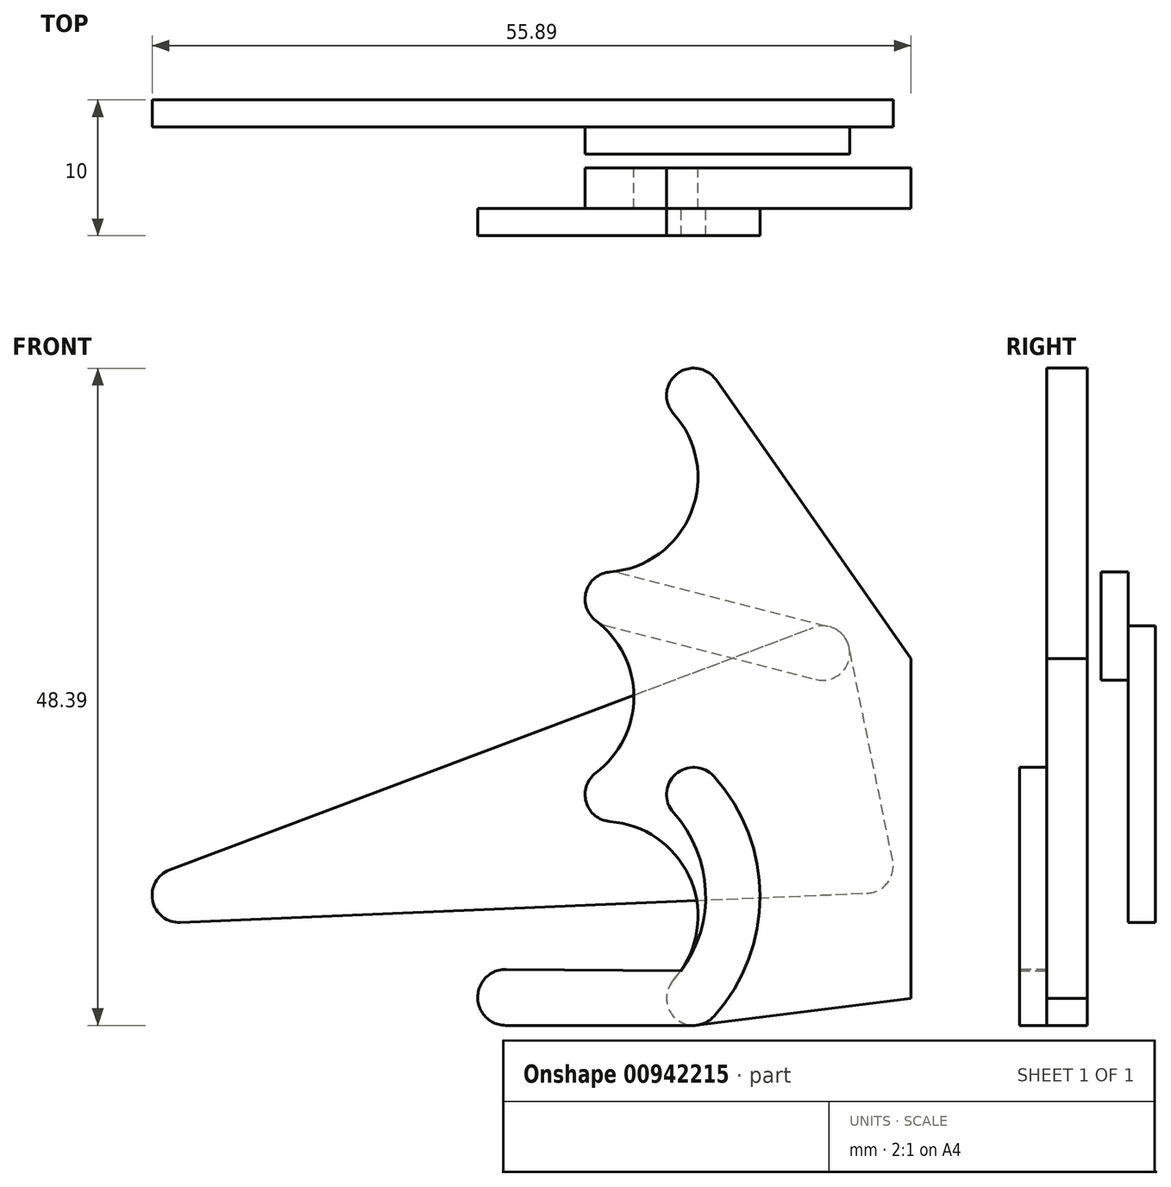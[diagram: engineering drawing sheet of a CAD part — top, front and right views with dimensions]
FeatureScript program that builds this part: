
annotation { "Feature Type Name" : "Feature", "Feature Type Description" : "" }
export const myFeature = defineFeature(function(context is Context, id is Id, definition is map)
    precondition{}
    {
        {
            var Q0;
            Q0=qCreatedBy(makeId("Front.planeOp"),FACE);
            var sketch = newSketch(context, id + "F0", { "sketchPlane" : qUnion([Q0])});
            skLineSegment(sketch, "E0", {"start": v(-16, 0) * mm, "end": v(-22, 29.4) * mm});
            skLineSegment(sketch, "E1", {"start": v(-22, 29.4) * mm, "end": v(-6.5, 25.41) * mm});
            skLineSegment(sketch, "E2", {"start": v(-6.5, 25.41) * mm, "end": v(-3.3, 9.74) * mm});
            skLineSegment(sketch, "E3", {"start": v(-3.3, 9.74) * mm, "end": v(-16, 0) * mm});
            skCircle(sketch, "E4", {"center": v(-22, 29.4) * mm, "radius": 16 * mm, "construction": true});
            skCircle(sketch, "E5", {"center": v(-16, 0) * mm, "radius": 16 * mm, "construction": true});
            skLineSegment(sketch, "E6", {"start": v(-13.54, 15.81) * mm, "end": v(-1.08, 5.78) * mm, "construction": true});
            skLineSegment(sketch, "E7", {"start": v(-6.5, 25.41) * mm, "end": v(-53.9, 7.57) * mm});
            skLineSegment(sketch, "E8", {"start": v(-53.9, 7.57) * mm, "end": v(-3.3, 9.74) * mm});
            skLineSegment(sketch, "E9", {"start": v(-53.9, 7.57) * mm, "end": v(-19, 14.7) * mm, "construction": true});
            skSolve(sketch);
        }
        {
            var Q0;
            Q0=qCreatedBy(makeId("Front.planeOp"),FACE);
            var sketch = newSketch(context, id + "F1", { "sketchPlane" : qUnion([Q0])});
            skCircle(sketch, "E10", {"center": v(-22, 29.4) * mm, "radius": 2 * mm});
            skCircle(sketch, "E11", {"center": v(-6.5, 25.41) * mm, "radius": 2 * mm});
            skCircle(sketch, "E12", {"center": v(-3.3, 9.74) * mm, "radius": 2 * mm});
            skCircle(sketch, "E13", {"center": v(-16, 0) * mm, "radius": 2 * mm});
            skLineSegment(sketch, "E14", {"start": v(-21.5, 31.33) * mm, "end": v(-6, 27.35) * mm});
            skLineSegment(sketch, "E15", {"start": v(-22.5, 27.46) * mm, "end": v(-7, 23.48) * mm});
            skSolve(sketch);
        }
        {
            var Q0;
            {var subQ0=sQuery(id+"F1.wireOp",EDGE,"E10");var subQ1=makeQuery(id+"F1.imprint","INTERSECT",VERTEX,{"derivedFrom":[subQ0,sQuery(id+"F1.wireOp",EDGE,"E14")]});Q0=makeQuery(id+"F1.imprint","IMPRINT",FACE,{"disambiguationData":[TD([[makeQuery(id+"F1.imprint","IMPRINT",EDGE,{"disambiguationData":[TD([[subQ1,-1.0]])],"derivedFrom":subQ0}),1.0]])]});}
            var Q1;
            {var subQ0=sQuery(id+"F1.wireOp",EDGE,"E11");var subQ1=makeQuery(id+"F1.imprint","INTERSECT",VERTEX,{"derivedFrom":[subQ0,sQuery(id+"F1.wireOp",EDGE,"E14")]});Q1=makeQuery(id+"F1.imprint","IMPRINT",FACE,{"disambiguationData":[TD([[makeQuery(id+"F1.imprint","IMPRINT",EDGE,{"disambiguationData":[TD([[subQ1,-1.0]])],"derivedFrom":subQ0}),1.0]])]});}
            var Q2;
            {var subQ0=sQuery(id+"F1.wireOp",EDGE,"E14");Q2=makeQuery(id+"F1.imprint","IMPRINT",FACE,{"disambiguationData":[TD([[makeQuery(id+"F1.imprint","IMPRINT",EDGE,{"derivedFrom":subQ0}),-1.0]])]});}
            extrude(context, id + "F2", {"entities" : qUnion([Q0, Q1, Q2]), "depth" : 2 * mm, "offsetDistance" : 25 * mm});
        }
        {
            var Q0;
            Q0=qCreatedBy(makeId("Front.planeOp"),FACE);
            var sketch = newSketch(context, id + "F3", { "sketchPlane" : qUnion([Q0])});
            skCircle(sketch, "E16", {"center": v(-6.5, 25.41) * mm, "radius": 2 * mm});
            skCircle(sketch, "E17", {"center": v(-3.3, 9.74) * mm, "radius": 2 * mm});
            skLineSegment(sketch, "E18", {"start": v(-1.34, 10.14) * mm, "end": v(-4.54, 25.81) * mm});
            skCircle(sketch, "E19", {"center": v(-53.9, 7.57) * mm, "radius": 2 * mm});
            skLineSegment(sketch, "E20", {"start": v(-54.6, 9.45) * mm, "end": v(-7.2, 27.28) * mm});
            skLineSegment(sketch, "E21", {"start": v(-53.8, 5.58) * mm, "end": v(-3.22, 7.74) * mm});
            skSolve(sketch);
        }
        {
            var Q0;
            Q0 = qSketchRegion(id + "F3", true);
            extrude(context, id + "F4", {"entities" : qUnion([Q0]), "oppositeDirection" : true, "depth" : 2 * mm, "offsetDistance" : 25 * mm});
        }
        {
            var Q0;
            Q0=qCreatedBy(makeId("Right.planeOp"),FACE);
            var Q1;
            Q1=sQuery(id+"F0.wireOp",VERTEX,"E0.end");
            cPlane(context, id + "F5", {"entities" : qUnion([Q0, Q1]), "cplaneType" : CPlaneType.PLANE_POINT, "offset" : 25 * mm, "width" : 150 * mm, "height" : 150 * mm});
        }
        {
            var Q0;
            Q0=qCreatedBy(makeId("Front.planeOp"),FACE);
            var sketch = newSketch(context, id + "F6", { "sketchPlane" : qUnion([Q0])});
            skCircle(sketch, "E22.0", {"center": v(-16, 0) * mm, "radius": 2 * mm});
            skCircle(sketch, "E22.1", {"center": v(-22, 29.4) * mm, "radius": 2 * mm});
            skCircle(sketch, "E23", {"center": v(-22, 15) * mm, "radius": 2 * mm});
            skLineSegment(sketch, "E24", {"start": v(-22, 15) * mm, "end": v(-16, 44.4) * mm, "construction": true});
            skCircle(sketch, "E25", {"center": v(-16, 44.4) * mm, "radius": 2 * mm});
            skArc(sketch, "E26", {"start": v(-22.15, 31.39) * mm, "mid": v(-16.19, 35.77) * mm, "end": v(-17.49, 43.05) * mm});
            skArc(sketch, "E27", {"start": v(-23.2, 16.6) * mm, "mid": v(-20.4, 22.2) * mm, "end": v(-23.2, 27.8) * mm});
            skArc(sketch, "E28", {"start": v(-17.49, 1.34) * mm, "mid": v(-16.19, 8.63) * mm, "end": v(-22.15, 13) * mm});
            skLineSegment(sketch, "E29", {"start": v(-14.36, 45.54) * mm, "end": v(0, 25) * mm});
            skLineSegment(sketch, "E30", {"start": v(0, 25) * mm, "end": v(0, 0) * mm});
            skLineSegment(sketch, "E31", {"start": v(0, 0) * mm, "end": v(-15.75, -1.98) * mm});
            skSolve(sketch);
        }
        {
            var Q0;
            Q0 = qSketchRegion(id + "F6", true);
            extrude(context, id + "F7", {"entities" : qUnion([Q0]), "depth" : 3 * mm, "offsetDistance" : 25 * mm});
        }
        {
            var Q0;
            Q0=makeQuery(id+"F7.opExtrude","SWEPT_BODY",BODY,{"disambiguationData":[OSD([sQuery(id+"F6.wireOp",EDGE,"E22.0"),sQuery(id+"F6.wireOp",EDGE,"E22.1"),sQuery(id+"F6.wireOp",EDGE,"E23"),sQuery(id+"F6.wireOp",EDGE,"E25"),sQuery(id+"F6.wireOp",EDGE,"E26"),sQuery(id+"F6.wireOp",EDGE,"E27"),sQuery(id+"F6.wireOp",EDGE,"E28"),sQuery(id+"F6.wireOp",EDGE,"E29"),sQuery(id+"F6.wireOp",EDGE,"E30"),sQuery(id+"F6.wireOp",EDGE,"E31")])]});
            var Q1;
            Q1=makeQuery(id+"F7.opExtrude","SWEPT_EDGE",EDGE,{"disambiguationData":[OSD([sQuery(id+"F6.wireOp",EDGE,"E30"),sQuery(id+"F6.wireOp",EDGE,"E31")])]});
            transform(context, id + "F8", {"entities" : qUnion([Q0]), "transformType" : TransformType.TRANSLATION_ENTITY, "oppositeDirectionEntity" : true, "transformLine" : qUnion([Q1]), "makeCopy" : false});
        }
        {
            var Q0;
            Q0=makeQuery(id+"F7.opExtrude","CAP_FACE",FACE,{"disambiguationData":[OSD([sQuery(id+"F6.wireOp",EDGE,"E22.0"),sQuery(id+"F6.wireOp",EDGE,"E22.1"),sQuery(id+"F6.wireOp",EDGE,"E23"),sQuery(id+"F6.wireOp",EDGE,"E25"),sQuery(id+"F6.wireOp",EDGE,"E26"),sQuery(id+"F6.wireOp",EDGE,"E27"),sQuery(id+"F6.wireOp",EDGE,"E28"),sQuery(id+"F6.wireOp",EDGE,"E29"),sQuery(id+"F6.wireOp",EDGE,"E30"),sQuery(id+"F6.wireOp",EDGE,"E31")])],"isStart":false});
            var sketch = newSketch(context, id + "F9", { "sketchPlane" : qUnion([Q0])});
            skCircle(sketch, "E32.0", {"center": v(-16, 0) * mm, "radius": 2 * mm});
            skCircle(sketch, "E32.1", {"center": v(-16, 15) * mm, "radius": 2 * mm});
            skArc(sketch, "E32.2", {"start": v(-17.49, 1.34) * mm, "mid": v(-15.12, 7.5) * mm, "end": v(-17.49, 13.66) * mm});
            skArc(sketch, "E33", {"start": v(-14.51, -1.34) * mm, "mid": v(-11.12, 7.5) * mm, "end": v(-14.51, 16.34) * mm});
            skLineSegment(sketch, "E34", {"start": v(-16, 15) * mm, "end": v(-16, 0) * mm, "construction": true});
            skSolve(sketch);
        }
        {
            var Q0;
            Q0 = qSketchRegion(id + "F9", true);
            extrude(context, id + "F10", {"entities" : qUnion([Q0]), "depth" : 2 * mm, "offsetDistance" : 25 * mm});
        }
        {
            var Q0;
            Q0=makeQuery(id+"F10.opExtrude","CAP_FACE",FACE,{"disambiguationData":[OSD([sQuery(id+"F9.wireOp",EDGE,"E32.0"),sQuery(id+"F9.wireOp",EDGE,"E32.1"),sQuery(id+"F9.wireOp",EDGE,"E32.2"),sQuery(id+"F9.wireOp",EDGE,"E33")])],"isStart":false});
            var sketch = newSketch(context, id + "F11", { "sketchPlane" : qUnion([Q0])});
            skLineSegment(sketch, "E35", {"start": v(-16, -2) * mm, "end": v(-29.85, -2) * mm});
            skLineSegment(sketch, "E36", {"start": v(-29.83, 2.13) * mm, "end": v(-15.98, 2) * mm});
            skLineSegment(sketch, "E37", {"start": v(-15.98, 2) * mm, "end": v(-16, -2) * mm});
            skCircle(sketch, "E38", {"center": v(-29.85, 0.06) * mm, "radius": 2.06 * mm});
            skSolve(sketch);
        }
        {
            var Q0;
            Q0 = qSketchRegion(id + "F11", true);
            var Q1;
            Q1=makeQuery(id+"F7.opExtrude","CAP_FACE",FACE,{"disambiguationData":[OSD([sQuery(id+"F6.wireOp",EDGE,"E22.0"),sQuery(id+"F6.wireOp",EDGE,"E22.1"),sQuery(id+"F6.wireOp",EDGE,"E23"),sQuery(id+"F6.wireOp",EDGE,"E25"),sQuery(id+"F6.wireOp",EDGE,"E26"),sQuery(id+"F6.wireOp",EDGE,"E27"),sQuery(id+"F6.wireOp",EDGE,"E28"),sQuery(id+"F6.wireOp",EDGE,"E29"),sQuery(id+"F6.wireOp",EDGE,"E30"),sQuery(id+"F6.wireOp",EDGE,"E31")])],"isStart":false});
            extrude(context, id + "F12", {"entities" : qUnion([Q0]), "operationType" : NewBodyOperationType.ADD, "endBound" : BoundingType.UP_TO_SURFACE, "oppositeDirection" : true, "depth" : 25 * mm, "endBoundEntityFace" : qUnion([Q1]), "offsetDistance" : 25 * mm});
        }
    });
